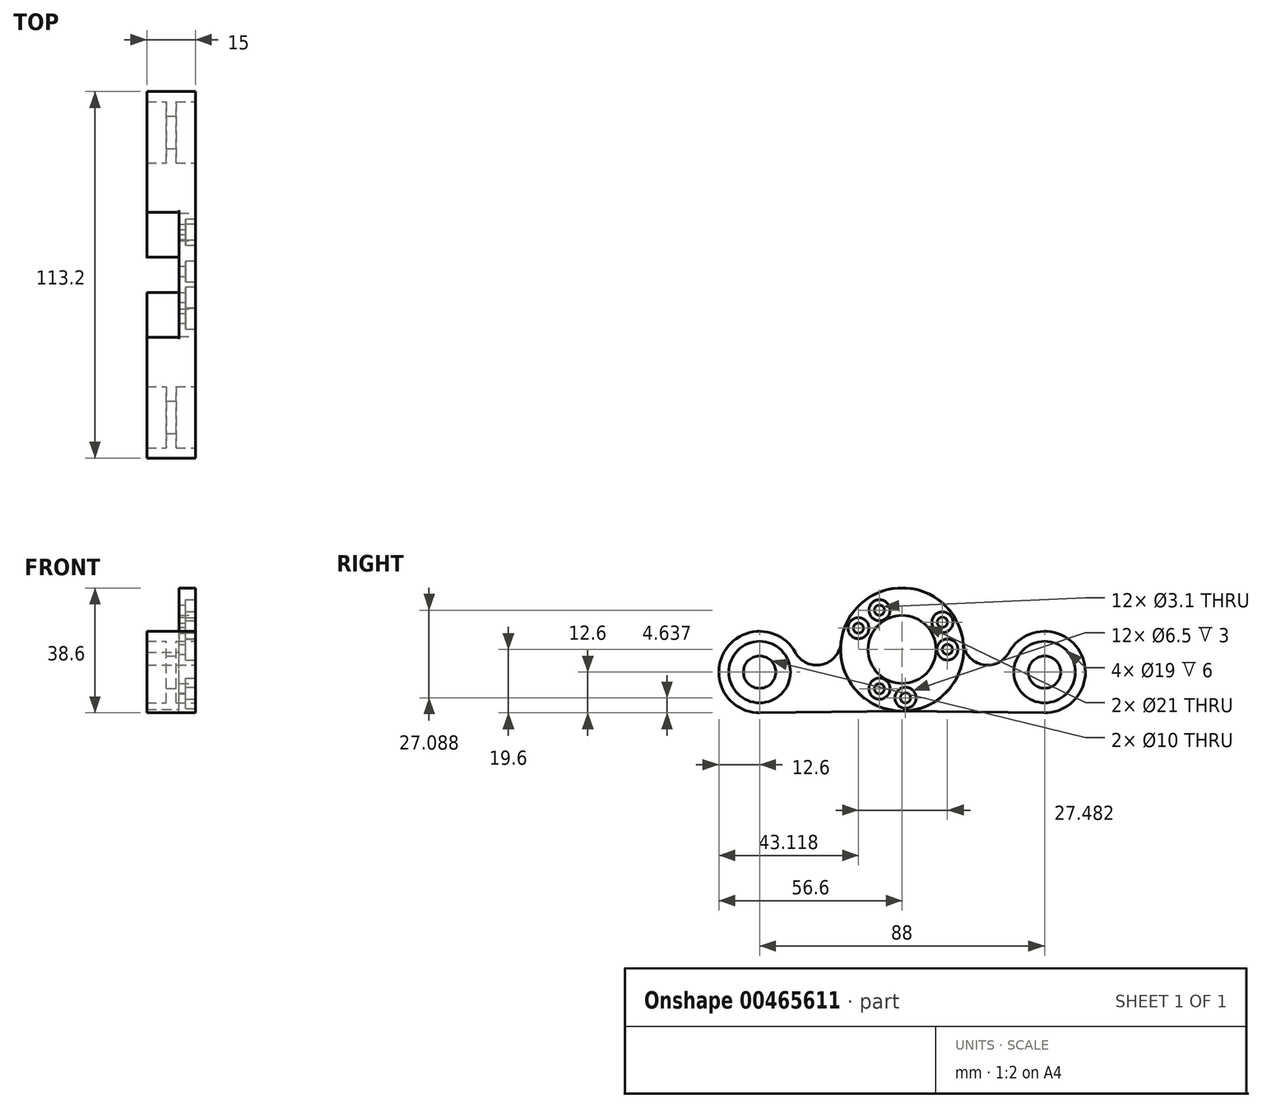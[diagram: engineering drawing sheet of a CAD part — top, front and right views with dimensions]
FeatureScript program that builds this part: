
annotation { "Feature Type Name" : "Feature", "Feature Type Description" : "" }
export const myFeature = defineFeature(function(context is Context, id is Id, definition is map)
    precondition{}
    {
        {
            var Q0;
            Q0=qCreatedBy(makeId("Right.planeOp"),FACE);
            var sketch = newSketch(context, id + "F0", { "sketchPlane" : qUnion([Q0])});
            skLineSegment(sketch, "E0", {"start": v(0, 0) * mm, "end": v(-44, -7) * mm});
            skCircle(sketch, "E1", {"center": v(-44, -7) * mm, "radius": 9.5 * mm});
            skLineSegment(sketch, "E2", {"start": v(0, 0) * mm, "end": v(0, 9.24) * mm, "construction": true});
            skCircle(sketch, "E3", {"center": v(0, 0) * mm, "radius": 26.26 * mm});
            skCircle(sketch, "E4", {"center": v(0, 9.24) * mm, "radius": 35.5 * mm, "construction": true});
            skLineSegment(sketch, "E5", {"start": v(-44, -7) * mm, "end": v(0, -7) * mm, "construction": true});
            skCircle(sketch, "E6", {"center": v(0, 0) * mm, "radius": 15 * mm});
            skCircle(sketch, "E7", {"center": v(0, 0) * mm, "radius": 14 * mm});
            skLineSegment(sketch, "E8", {"start": v(0, 0) * mm, "end": v(14, 0) * mm, "construction": true});
            skLineSegment(sketch, "E9", {"start": v(0, 0) * mm, "end": v(12.44, 8.39) * mm, "construction": true});
            skCircle(sketch, "E10", {"center": v(0, 0) * mm, "radius": 19 * mm});
            skSolve(sketch);
        }
        {
            var Q0;
            Q0=qCreatedBy(makeId("Right.planeOp"),FACE);
            var sketch = newSketch(context, id + "F1", { "sketchPlane" : qUnion([Q0])});
            skArc(sketch, "E11", {"start": v(0.26, -19) * mm, "mid": v(14, 12.84) * mm, "end": v(-18.9, 1.9) * mm});
            skArc(sketch, "E12", {"start": v(-32.95, -0.95) * mm, "mid": v(-54.88, -0.65) * mm, "end": v(-43.83, -19.6) * mm});
            skLineSegment(sketch, "E13", {"start": v(0.26, -19) * mm, "end": v(-43.83, -19.6) * mm});
            skArc(sketch, "E14", {"start": v(-32.95, -0.95) * mm, "mid": v(-24.88, -4.7) * mm, "end": v(-18.9, 1.9) * mm});
            skCircle(sketch, "E15", {"center": v(-44, -7) * mm, "radius": 9.6 * mm});
            skCircle(sketch, "E16", {"center": v(0, 0) * mm, "radius": 10.5 * mm});
            skSolve(sketch);
        }
        {
            var Q0;
            Q0 = qSketchRegion(id + "F1", true);
            extrude(context, id + "F2", {"entities" : qUnion([Q0]), "oppositeDirection" : true, "depth" : 5 * mm});
        }
        {
            var Q0;
            Q0=qCreatedBy(makeId("Right.planeOp"),FACE);
            var sketch = newSketch(context, id + "F3", { "sketchPlane" : qUnion([Q0])});
            skCircle(sketch, "E17", {"center": v(-44, -7) * mm, "radius": 12.6 * mm});
            skCircle(sketch, "E18", {"center": v(-44, -7) * mm, "radius": 9.5 * mm});
            skSolve(sketch);
        }
        {
            var Q0;
            Q0=makeQuery(id+"F3.imprint","IMPRINT",FACE,{"disambiguationData":[TD([[makeQuery(id+"F3.imprint","IMPRINT",EDGE,{"derivedFrom":sQuery(id+"F3.wireOp",EDGE,"E17")}),1.0]])]});
            extrude(context, id + "F4", {"entities" : qUnion([Q0]), "operationType" : NewBodyOperationType.ADD, "oppositeDirection" : true, "depth" : 15 * mm});
        }
        {
            var Q0;
            Q0=makeQuery(id+"F2.opExtrude","CAP_FACE",FACE,{"disambiguationData":[OSD([sQuery(id+"F1.wireOp",EDGE,"E11"),sQuery(id+"F1.wireOp",EDGE,"E12"),sQuery(id+"F1.wireOp",EDGE,"E13"),sQuery(id+"F1.wireOp",EDGE,"E14"),sQuery(id+"F1.wireOp",EDGE,"2yqbEohW-cPEA-sn5k-uTFb-EA6Qo4XhDF0H"),sQuery(id+"F1.wireOp",EDGE,"E15"),sQuery(id+"F1.wireOp",EDGE,"E16")])],"isStart":false});
            var sketch = newSketch(context, id + "F5", { "sketchPlane" : qUnion([Q0])});
            skArc(sketch, "E19.0", {"start": v(32.95, -0.95) * mm, "mid": v(24.88, -4.7) * mm, "end": v(18.9, 1.9) * mm});
            skLineSegment(sketch, "E20.0", {"start": v(-0.26, -19) * mm, "end": v(43.83, -19.6) * mm});
            skArc(sketch, "E21.0", {"start": v(32.95, -0.95) * mm, "mid": v(33.12, -13.35) * mm, "end": v(43.83, -19.6) * mm});
            skArc(sketch, "E22", {"start": v(-0.26, -19) * mm, "mid": v(14, -12.84) * mm, "end": v(18.9, 1.9) * mm});
            skSolve(sketch);
        }
        {
            var Q0;
            Q0 = qSketchRegion(id + "F5", true);
            var Q1;
            Q1=makeQuery(id+"F4.opExtrude","CAP_FACE",FACE,{"disambiguationData":[OSD([sQuery(id+"F3.wireOp",EDGE,"E17"),sQuery(id+"F3.wireOp",EDGE,"E18")])],"isStart":false});
            extrude(context, id + "F6", {"entities" : qUnion([Q0]), "operationType" : NewBodyOperationType.ADD, "endBound" : BoundingType.UP_TO_SURFACE, "depth" : 25 * mm, "endBoundEntityFace" : qUnion([Q1]), "offsetDistance" : 25 * mm});
        }
        {
            var Q0;
            Q0=makeQuery(id+"F6.opExtrude","SWEPT_EDGE",EDGE,{"disambiguationData":[OSD([sQuery(id+"F1.wireOp",EDGE,"E11"),sQuery(id+"F5.wireOp",EDGE,"E19.0"),sQuery(id+"F5.wireOp",EDGE,"E22")])]});
            var Q1;
            Q1=makeQuery(id+"F6.opExtrude","SWEPT_EDGE",EDGE,{"disambiguationData":[OSD([sQuery(id+"F1.wireOp",EDGE,"E11"),sQuery(id+"F5.wireOp",EDGE,"f37111b8-7552-4d3e-a611-02c1443501aa.0"),sQuery(id+"F5.wireOp",EDGE,"E22")])]});
            fillet(context, id + "F7", {"entities" : qUnion([Q0, Q1]), "radius" : 0.5 * mm, "tangentPropagation" : true, "allowEdgeOverflow" : false});
        }
        {
            var Q0;
            Q0=makeQuery(id+"F2.opExtrude","CAP_FACE",FACE,{"disambiguationData":[OSD([sQuery(id+"F1.wireOp",EDGE,"E11"),sQuery(id+"F1.wireOp",EDGE,"E12"),sQuery(id+"F1.wireOp",EDGE,"tDpK871F-h2di-iHeD-UTMA-PbM8zHeAsH1Q"),sQuery(id+"F1.wireOp",EDGE,"E13"),sQuery(id+"F1.wireOp",EDGE,"E14"),sQuery(id+"F1.wireOp",EDGE,"2yqbEohW-cPEA-sn5k-uTFb-EA6Qo4XhDF0H"),sQuery(id+"F1.wireOp",EDGE,"E15"),sQuery(id+"F1.wireOp",EDGE,"E16")])],"isStart":false});
            var sketch = newSketch(context, id + "F8", { "sketchPlane" : qUnion([Q0])});
            skCircle(sketch, "E23", {"center": v(0, 0) * mm, "radius": 19.3 * mm});
            skSolve(sketch);
        }
        {
            var Q0;
            Q0 = qSketchRegion(id + "F8", true);
            extrude(context, id + "F9", {"entities" : qUnion([Q0]), "operationType" : NewBodyOperationType.REMOVE, "depth" : 25 * mm});
        }
        {
            var Q0;
            Q0=makeQuery(id+"F2.opExtrude","CAP_FACE",FACE,{"disambiguationData":[OSD([sQuery(id+"F1.wireOp",EDGE,"E11"),sQuery(id+"F1.wireOp",EDGE,"E12"),sQuery(id+"F1.wireOp",EDGE,"tDpK871F-h2di-iHeD-UTMA-PbM8zHeAsH1Q"),sQuery(id+"F1.wireOp",EDGE,"E13"),sQuery(id+"F1.wireOp",EDGE,"E14"),sQuery(id+"F1.wireOp",EDGE,"2yqbEohW-cPEA-sn5k-uTFb-EA6Qo4XhDF0H"),sQuery(id+"F1.wireOp",EDGE,"E15"),sQuery(id+"F1.wireOp",EDGE,"E16")])],"isStart":true});
            var Q1;
            Q1=makeQuery(id+"F12.boolean.opBoolean","MERGE",FACE,{"derivedFrom":[makeQuery(id+"F4.opExtrude","CAP_FACE",FACE,{"disambiguationData":[OSD([sQuery(id+"F3.wireOp",EDGE,"E17"),sQuery(id+"F3.wireOp",EDGE,"E18")])],"isStart":false}),makeQuery(id+"F12.opExtrude","CAP_FACE",FACE,{"disambiguationData":[OSD([sQuery(id+"F11.wireOp",EDGE,"M0L3tIGM-rfNj-AuJK-nCgh-wAJp0PGvIRna"),sQuery(id+"F11.wireOp",EDGE,"E24")])],"isStart":true})]});
            cPlane(context, id + "F10", {"entities" : qUnion([Q0, Q1]), "cplaneType" : CPlaneType.MID_PLANE, "offset" : 25 * mm, "width" : 150 * mm, "height" : 150 * mm});
        }
        {
            var Q0;
            Q0=qCreatedBy(id+"F10.planeOp",FACE);
            var sketch = newSketch(context, id + "F11", { "sketchPlane" : qUnion([Q0])});
            skCircle(sketch, "E24", {"center": v(-44, -7) * mm, "radius": 5 * mm});
            skCircle(sketch, "E25.0", {"center": v(-44, -7) * mm, "radius": 9.5 * mm});
            skSolve(sketch);
        }
        {
            var Q0;
            Q0=makeQuery(id+"F11.imprint","IMPRINT",FACE,{"disambiguationData":[TD([[makeQuery(id+"F11.imprint","IMPRINT",EDGE,{"derivedFrom":sQuery(id+"F11.wireOp",EDGE,"M0L3tIGM-rfNj-AuJK-nCgh-wAJp0PGvIRna")}),1.0]])]});
            var Q1;
            Q1=makeQuery(id+"F11.imprint","IMPRINT",FACE,{"disambiguationData":[TD([[makeQuery(id+"F11.imprint","IMPRINT",EDGE,{"derivedFrom":sQuery(id+"F11.wireOp",EDGE,"E24")}),-1.0]])]});
            var Q2;
            Q2=makeQuery(id+"F2.opExtrude","CAP_FACE",FACE,{"disambiguationData":[OSD([sQuery(id+"F1.wireOp",EDGE,"E11"),sQuery(id+"F1.wireOp",EDGE,"E12"),sQuery(id+"F1.wireOp",EDGE,"tDpK871F-h2di-iHeD-UTMA-PbM8zHeAsH1Q"),sQuery(id+"F1.wireOp",EDGE,"E13"),sQuery(id+"F1.wireOp",EDGE,"E14"),sQuery(id+"F1.wireOp",EDGE,"2yqbEohW-cPEA-sn5k-uTFb-EA6Qo4XhDF0H"),sQuery(id+"F1.wireOp",EDGE,"E15"),sQuery(id+"F1.wireOp",EDGE,"E16")])],"isStart":true});
            extrude(context, id + "F12", {"entities" : qUnion([Q0, Q1]), "operationType" : NewBodyOperationType.ADD, "endBound" : BoundingType.SYMMETRIC, "oppositeDirection" : true, "depth" : 3 * mm, "endBoundEntityFace" : qUnion([Q2]), "hasOffset" : true, "offsetDistance" : 3 * mm});
        }
        {
            var Q0;
            Q0=makeQuery(id+"F2.opExtrude","SWEPT_BODY",BODY,{"disambiguationData":[OSD([sQuery(id+"F1.wireOp",EDGE,"E11"),sQuery(id+"F1.wireOp",EDGE,"E12"),sQuery(id+"F1.wireOp",EDGE,"E13"),sQuery(id+"F1.wireOp",EDGE,"E14"),sQuery(id+"F1.wireOp",EDGE,"2yqbEohW-cPEA-sn5k-uTFb-EA6Qo4XhDF0H"),sQuery(id+"F1.wireOp",EDGE,"E15"),sQuery(id+"F1.wireOp",EDGE,"E16")])]});
            var Q1;
            Q1=qCreatedBy(makeId("Top.planeOp"),FACE);
            mirror(context, id + "F13", {"entities" : qUnion([Q0]), "mirrorPlane" : qUnion([Q1])});
        }
        {
            var Q0;
            Q0=qCreatedBy(makeId("Top.planeOp"),FACE);
            var sketch = newSketch(context, id + "F14", { "sketchPlane" : qUnion([Q0])});
            skLineSegment(sketch, "E26", {"start": v(0, 0) * mm, "end": v(-40.67, 0) * mm, "construction": true});
            skSolve(sketch);
        }
        {
            var Q0;
            Q0=makeQuery(id+"F13.opPattern","COPY",BODY,{"derivedFrom":makeQuery(id+"F2.opExtrude","SWEPT_BODY",BODY,{"disambiguationData":[OSD([sQuery(id+"F1.wireOp",EDGE,"E11"),sQuery(id+"F1.wireOp",EDGE,"E12"),sQuery(id+"F1.wireOp",EDGE,"E13"),sQuery(id+"F1.wireOp",EDGE,"E14"),sQuery(id+"F1.wireOp",EDGE,"2yqbEohW-cPEA-sn5k-uTFb-EA6Qo4XhDF0H"),sQuery(id+"F1.wireOp",EDGE,"E15"),sQuery(id+"F1.wireOp",EDGE,"E16")])]}),"instanceName":"1"});
            var Q1;
            Q1=sQuery(id+"F14.wireOp",EDGE,"E26");
            transform(context, id + "F15", {"entities" : qUnion([Q0]), "transformType" : TransformType.ROTATION, "transformAxis" : qUnion([Q1]), "angle" : 180 * degree, "makeCopy" : false});
        }
        {
            var Q0;
            Q0=qCreatedBy(makeId("Right.planeOp"),FACE);
            var sketch = newSketch(context, id + "F16", { "sketchPlane" : qUnion([Q0])});
            skCircle(sketch, "E27", {"center": v(0, 0) * mm, "radius": 15 * mm, "construction": true});
            skPoint(sketch, "E28", {"position": v(12.44, 8.39) * mm});
            skPoint(sketch, "E29.1.0", {"position": v(-13.48, 6.58) * mm});
            skPoint(sketch, "E29.2.0", {"position": v(1.05, -14.96) * mm});
            skCircle(sketch, "E30", {"center": v(0, 0) * mm, "radius": 14 * mm, "construction": true});
            skPoint(sketch, "E31", {"position": v(14, 0) * mm});
            skPoint(sketch, "E32.1.0", {"position": v(-7, 12.12) * mm});
            skPoint(sketch, "E32.2.0", {"position": v(-7, -12.12) * mm});
            skSolve(sketch);
        }
        {
            var Q0;
            Q0=sQuery(id+"F16.wireOp",VERTEX,"E28");
            var Q1;
            Q1=sQuery(id+"F16.wireOp",VERTEX,"E29.2.0");
            var Q2;
            Q2=sQuery(id+"F16.wireOp",VERTEX,"E29.1.0");
            var Q3;
            Q3=makeQuery(id+"F2.opExtrude","SWEPT_BODY",BODY,{"disambiguationData":[OSD([sQuery(id+"F1.wireOp",EDGE,"E11"),sQuery(id+"F1.wireOp",EDGE,"E12"),sQuery(id+"F1.wireOp",EDGE,"tDpK871F-h2di-iHeD-UTMA-PbM8zHeAsH1Q"),sQuery(id+"F1.wireOp",EDGE,"E13"),sQuery(id+"F1.wireOp",EDGE,"E14"),sQuery(id+"F1.wireOp",EDGE,"2yqbEohW-cPEA-sn5k-uTFb-EA6Qo4XhDF0H"),sQuery(id+"F1.wireOp",EDGE,"E15"),sQuery(id+"F1.wireOp",EDGE,"E16")])]});
            var Q4;
            Q4=makeQuery(id+"F13.opPattern","COPY",BODY,{"derivedFrom":makeQuery(id+"F2.opExtrude","SWEPT_BODY",BODY,{"disambiguationData":[OSD([sQuery(id+"F1.wireOp",EDGE,"E11"),sQuery(id+"F1.wireOp",EDGE,"E12"),sQuery(id+"F1.wireOp",EDGE,"E13"),sQuery(id+"F1.wireOp",EDGE,"E14"),sQuery(id+"F1.wireOp",EDGE,"2yqbEohW-cPEA-sn5k-uTFb-EA6Qo4XhDF0H"),sQuery(id+"F1.wireOp",EDGE,"E15"),sQuery(id+"F1.wireOp",EDGE,"E16")])]}),"instanceName":"1"});
            hole(context, id + "F17", {"style" : HoleStyle.C_BORE, "endStyle" : HoleEndStyle.THROUGH, "holeDiameter" : 3.1 * mm, "cBoreDiameter" : 6.5 * mm, "cBoreDepth" : 3 * mm, "isTappedThrough" : true, "tappedDepth" : 2.3 * mm, "tapClearance" : 3, "startFromSketch" : true, "locations" : qUnion([Q0, Q1, Q2]), "scope" : qUnion([Q3, Q4]), "majorDiameter" : 5 * mm});
        }
        {
            var Q0;
            Q0=sQuery(id+"F16.wireOp",VERTEX,"E31");
            var Q1;
            Q1=sQuery(id+"F16.wireOp",VERTEX,"E32.2.0");
            var Q2;
            Q2=sQuery(id+"F16.wireOp",VERTEX,"E32.1.0");
            var Q3;
            Q3=makeQuery(id+"F2.opExtrude","SWEPT_BODY",BODY,{"disambiguationData":[OSD([sQuery(id+"F1.wireOp",EDGE,"E11"),sQuery(id+"F1.wireOp",EDGE,"E12"),sQuery(id+"F1.wireOp",EDGE,"tDpK871F-h2di-iHeD-UTMA-PbM8zHeAsH1Q"),sQuery(id+"F1.wireOp",EDGE,"E13"),sQuery(id+"F1.wireOp",EDGE,"E14"),sQuery(id+"F1.wireOp",EDGE,"2yqbEohW-cPEA-sn5k-uTFb-EA6Qo4XhDF0H"),sQuery(id+"F1.wireOp",EDGE,"E15"),sQuery(id+"F1.wireOp",EDGE,"E16")])]});
            var Q4;
            Q4=makeQuery(id+"F13.opPattern","COPY",BODY,{"derivedFrom":makeQuery(id+"F2.opExtrude","SWEPT_BODY",BODY,{"disambiguationData":[OSD([sQuery(id+"F1.wireOp",EDGE,"E11"),sQuery(id+"F1.wireOp",EDGE,"E12"),sQuery(id+"F1.wireOp",EDGE,"E13"),sQuery(id+"F1.wireOp",EDGE,"E14"),sQuery(id+"F1.wireOp",EDGE,"2yqbEohW-cPEA-sn5k-uTFb-EA6Qo4XhDF0H"),sQuery(id+"F1.wireOp",EDGE,"E15"),sQuery(id+"F1.wireOp",EDGE,"E16")])]}),"instanceName":"1"});
            hole(context, id + "F18", {"style" : HoleStyle.C_BORE, "endStyle" : HoleEndStyle.THROUGH, "holeDiameter" : 3.1 * mm, "cBoreDiameter" : 6.5 * mm, "cBoreDepth" : 3 * mm, "isTappedThrough" : true, "tappedDepth" : 2.3 * mm, "tapClearance" : 3, "startFromSketch" : true, "locations" : qUnion([Q0, Q1, Q2]), "scope" : qUnion([Q3, Q4]), "majorDiameter" : 5 * mm});
        }
    });
